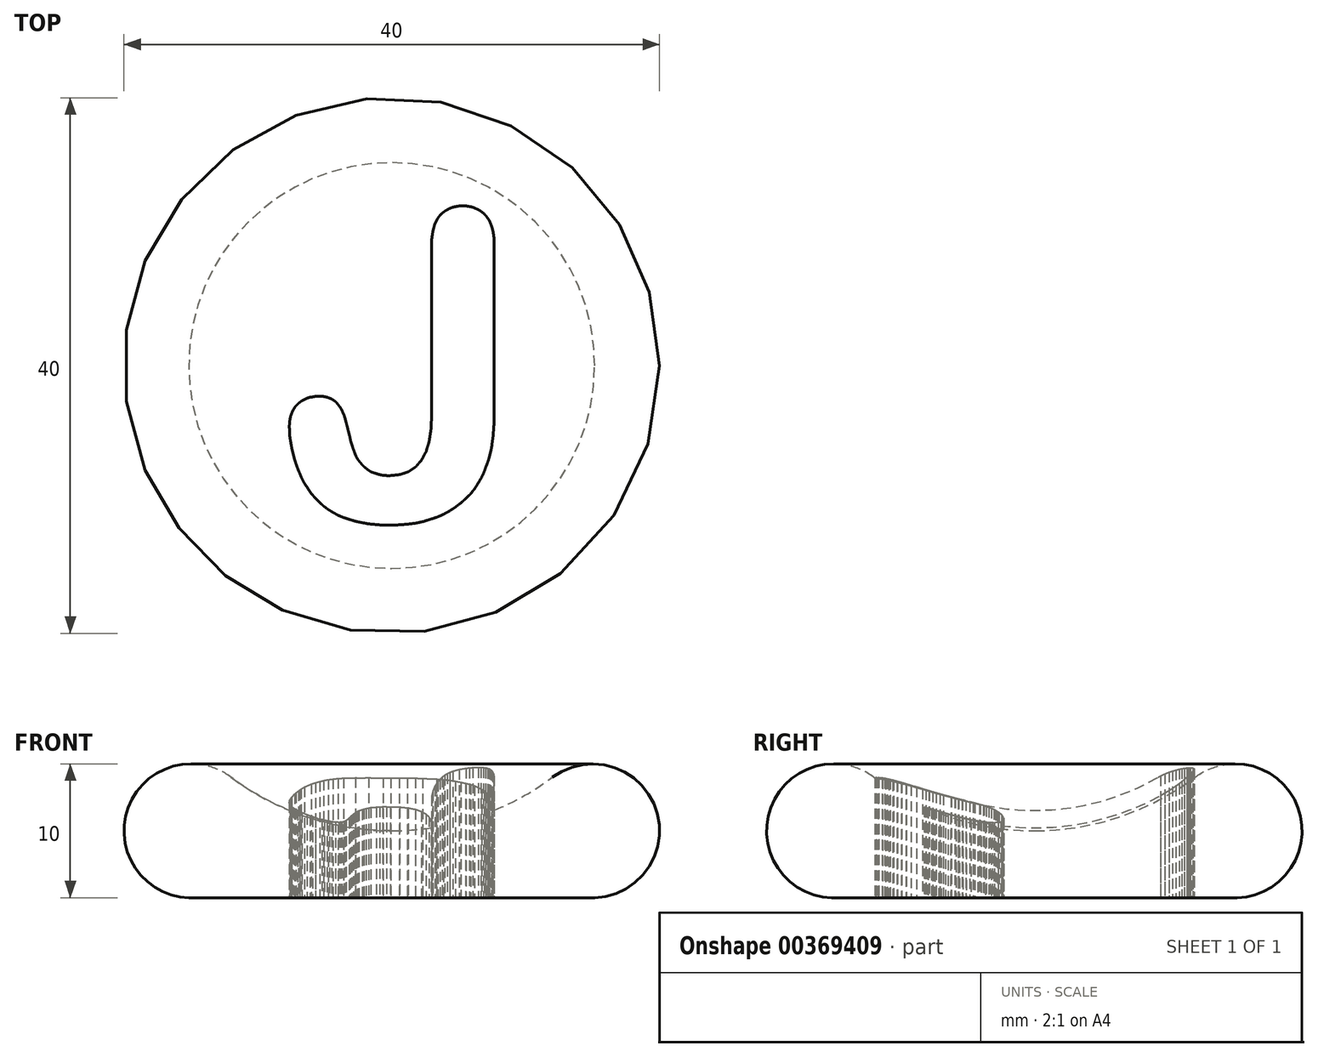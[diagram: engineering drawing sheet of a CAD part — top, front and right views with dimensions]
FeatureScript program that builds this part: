
annotation { "Feature Type Name" : "Feature", "Feature Type Description" : "" }
export const myFeature = defineFeature(function(context is Context, id is Id, definition is map)
    precondition{}
    {
        {
            var Q0;
            Q0=qCreatedBy(makeId("Front.planeOp"),FACE);
            var sketch = newSketch(context, id + "F0", { "sketchPlane" : qUnion([Q0])});
            skArc(sketch, "E0", {"start": v(-12, 9) * mm, "mid": v(-6.32, 6.03) * mm, "end": v(0, 5) * mm});
            skArc(sketch, "E1", {"start": v(-12, 9) * mm, "mid": v(-19.72, 6.65) * mm, "end": v(-15.16, 0) * mm});
            skLineSegment(sketch, "E2", {"start": v(-15.16, 0) * mm, "end": v(0, 0) * mm});
            skLineSegment(sketch, "E3", {"start": v(0, 5) * mm, "end": v(0, 0) * mm});
            skSolve(sketch);
        }
        {
            var Q0;
            Q0=makeQuery(id+"F0.imprint","IMPRINT",FACE,{"disambiguationData":[TD([[makeQuery(id+"F0.imprint","IMPRINT",EDGE,{"derivedFrom":sQuery(id+"F0.wireOp",EDGE,"E0")}),-1.0]])]});
            var Q1;
            Q1=sQuery(id+"F0.wireOp",EDGE,"E3");
            revolve(context, id + "F1", {"entities" : qUnion([Q0]), "axis" : qUnion([Q1]), "revolveType" : RevolveType.FULL});
        }
        {
            var Q0;
            Q0=qCreatedBy(makeId("Top.planeOp"),FACE);
            var sketch = newSketch(context, id + "F2", { "sketchPlane" : qUnion([Q0])});
            skLineSegment(sketch, "E4", {"start": v(-7.63, -4.3) * mm, "end": v(-7.6, -4.04) * mm});
            skLineSegment(sketch, "E5", {"start": v(-7.6, -4.04) * mm, "end": v(-7.56, -3.8) * mm});
            skLineSegment(sketch, "E6", {"start": v(-7.56, -3.8) * mm, "end": v(-7.49, -3.6) * mm});
            skLineSegment(sketch, "E7", {"start": v(-7.49, -3.6) * mm, "end": v(-7.4, -3.38) * mm});
            skLineSegment(sketch, "E8", {"start": v(-7.4, -3.38) * mm, "end": v(-7.3, -3.22) * mm});
            skLineSegment(sketch, "E9", {"start": v(-7.3, -3.22) * mm, "end": v(-7.18, -3.03) * mm});
            skLineSegment(sketch, "E10", {"start": v(-7.18, -3.03) * mm, "end": v(-7.04, -2.89) * mm});
            skLineSegment(sketch, "E11", {"start": v(-7.04, -2.89) * mm, "end": v(-6.87, -2.75) * mm});
            skLineSegment(sketch, "E12", {"start": v(-6.87, -2.75) * mm, "end": v(-6.7, -2.63) * mm});
            skLineSegment(sketch, "E13", {"start": v(-6.7, -2.63) * mm, "end": v(-6.52, -2.54) * mm});
            skLineSegment(sketch, "E14", {"start": v(-6.52, -2.54) * mm, "end": v(-6.33, -2.44) * mm});
            skLineSegment(sketch, "E15", {"start": v(-6.33, -2.44) * mm, "end": v(-6.12, -2.37) * mm});
            skLineSegment(sketch, "E16", {"start": v(-6.12, -2.37) * mm, "end": v(-5.9, -2.35) * mm});
            skLineSegment(sketch, "E17", {"start": v(-5.9, -2.35) * mm, "end": v(-5.7, -2.3) * mm});
            skLineSegment(sketch, "E18", {"start": v(-5.7, -2.3) * mm, "end": v(-5.46, -2.3) * mm});
            skLineSegment(sketch, "E19", {"start": v(-5.46, -2.3) * mm, "end": v(-5.22, -2.3) * mm});
            skLineSegment(sketch, "E20", {"start": v(-5.22, -2.3) * mm, "end": v(-5.01, -2.32) * mm});
            skLineSegment(sketch, "E21", {"start": v(-5.01, -2.32) * mm, "end": v(-4.82, -2.37) * mm});
            skLineSegment(sketch, "E22", {"start": v(-4.82, -2.37) * mm, "end": v(-4.63, -2.44) * mm});
            skLineSegment(sketch, "E23", {"start": v(-4.63, -2.44) * mm, "end": v(-4.47, -2.51) * mm});
            skLineSegment(sketch, "E24", {"start": v(-4.47, -2.51) * mm, "end": v(-4.33, -2.6) * mm});
            skLineSegment(sketch, "E25", {"start": v(-4.33, -2.6) * mm, "end": v(-4.19, -2.7) * mm});
            skLineSegment(sketch, "E26", {"start": v(-4.19, -2.7) * mm, "end": v(-4.07, -2.84) * mm});
            skLineSegment(sketch, "E27", {"start": v(-4.07, -2.84) * mm, "end": v(-3.95, -2.98) * mm});
            skLineSegment(sketch, "E28", {"start": v(-3.95, -2.98) * mm, "end": v(-3.83, -3.15) * mm});
            skLineSegment(sketch, "E29", {"start": v(-3.83, -3.15) * mm, "end": v(-3.74, -3.31) * mm});
            skLineSegment(sketch, "E30", {"start": v(-3.74, -3.31) * mm, "end": v(-3.64, -3.53) * mm});
            skLineSegment(sketch, "E31", {"start": v(-3.64, -3.53) * mm, "end": v(-3.55, -3.74) * mm});
            skLineSegment(sketch, "E32", {"start": v(-3.55, -3.74) * mm, "end": v(-3.48, -3.97) * mm});
            skLineSegment(sketch, "E33", {"start": v(-3.48, -3.97) * mm, "end": v(-3.4, -4.23) * mm});
            skLineSegment(sketch, "E34", {"start": v(-3.4, -4.23) * mm, "end": v(-3.34, -4.52) * mm});
            skLineSegment(sketch, "E35", {"start": v(-3.34, -4.52) * mm, "end": v(-3.27, -4.8) * mm});
            skLineSegment(sketch, "E36", {"start": v(-3.27, -4.8) * mm, "end": v(-3.2, -5.08) * mm});
            skLineSegment(sketch, "E37", {"start": v(-3.2, -5.08) * mm, "end": v(-3.12, -5.34) * mm});
            skLineSegment(sketch, "E38", {"start": v(-3.12, -5.34) * mm, "end": v(-3.08, -5.6) * mm});
            skLineSegment(sketch, "E39", {"start": v(-3.08, -5.6) * mm, "end": v(-3, -5.84) * mm});
            skLineSegment(sketch, "E40", {"start": v(-3, -5.84) * mm, "end": v(-2.94, -6.05) * mm});
            skLineSegment(sketch, "E41", {"start": v(-2.94, -6.05) * mm, "end": v(-2.87, -6.26) * mm});
            skLineSegment(sketch, "E42", {"start": v(-2.87, -6.26) * mm, "end": v(-2.8, -6.45) * mm});
            skLineSegment(sketch, "E43", {"start": v(-2.8, -6.45) * mm, "end": v(-2.72, -6.64) * mm});
            skLineSegment(sketch, "E44", {"start": v(-2.72, -6.64) * mm, "end": v(-2.65, -6.8) * mm});
            skLineSegment(sketch, "E45", {"start": v(-2.65, -6.8) * mm, "end": v(-2.56, -6.97) * mm});
            skLineSegment(sketch, "E46", {"start": v(-2.56, -6.97) * mm, "end": v(-2.44, -7.13) * mm});
            skLineSegment(sketch, "E47", {"start": v(-2.44, -7.13) * mm, "end": v(-2.32, -7.28) * mm});
            skLineSegment(sketch, "E48", {"start": v(-2.32, -7.28) * mm, "end": v(-2.2, -7.42) * mm});
            skLineSegment(sketch, "E49", {"start": v(-2.2, -7.42) * mm, "end": v(-2.06, -7.56) * mm});
            skLineSegment(sketch, "E50", {"start": v(-2.06, -7.56) * mm, "end": v(-1.9, -7.7) * mm});
            skLineSegment(sketch, "E51", {"start": v(-1.9, -7.7) * mm, "end": v(-1.73, -7.82) * mm});
            skLineSegment(sketch, "E52", {"start": v(-1.73, -7.82) * mm, "end": v(-1.57, -7.94) * mm});
            skLineSegment(sketch, "E53", {"start": v(-1.57, -7.94) * mm, "end": v(-1.36, -8) * mm});
            skLineSegment(sketch, "E54", {"start": v(-1.36, -8) * mm, "end": v(-1.14, -8.08) * mm});
            skLineSegment(sketch, "E55", {"start": v(-1.14, -8.08) * mm, "end": v(-0.9, -8.15) * mm});
            skLineSegment(sketch, "E56", {"start": v(-0.9, -8.15) * mm, "end": v(-0.67, -8.2) * mm});
            skLineSegment(sketch, "E57", {"start": v(-0.67, -8.2) * mm, "end": v(-0.39, -8.22) * mm});
            skLineSegment(sketch, "E58", {"start": v(-0.39, -8.22) * mm, "end": v(-0.1, -8.22) * mm});
            skLineSegment(sketch, "E59", {"start": v(-0.1, -8.22) * mm, "end": v(0.6, -8.15) * mm});
            skLineSegment(sketch, "E60", {"start": v(0.6, -8.15) * mm, "end": v(1.24, -7.94) * mm});
            skLineSegment(sketch, "E61", {"start": v(1.24, -7.94) * mm, "end": v(1.78, -7.58) * mm});
            skLineSegment(sketch, "E62", {"start": v(1.78, -7.58) * mm, "end": v(2.2, -7.09) * mm});
            skLineSegment(sketch, "E63", {"start": v(2.2, -7.09) * mm, "end": v(2.56, -6.45) * mm});
            skLineSegment(sketch, "E64", {"start": v(2.56, -6.45) * mm, "end": v(2.8, -5.67) * mm});
            skLineSegment(sketch, "E65", {"start": v(2.8, -5.67) * mm, "end": v(2.94, -4.73) * mm});
            skLineSegment(sketch, "E66", {"start": v(2.94, -4.73) * mm, "end": v(2.98, -3.67) * mm});
            skLineSegment(sketch, "E67", {"start": v(2.98, -3.67) * mm, "end": v(2.98, 9.1) * mm});
            skLineSegment(sketch, "E68", {"start": v(2.98, 9.1) * mm, "end": v(2.98, 9.42) * mm});
            skLineSegment(sketch, "E69", {"start": v(2.98, 9.42) * mm, "end": v(3.03, 9.75) * mm});
            skLineSegment(sketch, "E70", {"start": v(3.03, 9.75) * mm, "end": v(3.08, 10.06) * mm});
            skLineSegment(sketch, "E71", {"start": v(3.08, 10.06) * mm, "end": v(3.15, 10.32) * mm});
            skLineSegment(sketch, "E72", {"start": v(3.15, 10.32) * mm, "end": v(3.22, 10.58) * mm});
            skLineSegment(sketch, "E73", {"start": v(3.22, 10.58) * mm, "end": v(3.34, 10.81) * mm});
            skLineSegment(sketch, "E74", {"start": v(3.34, 10.81) * mm, "end": v(3.46, 11.03) * mm});
            skLineSegment(sketch, "E75", {"start": v(3.46, 11.03) * mm, "end": v(3.6, 11.21) * mm});
            skLineSegment(sketch, "E76", {"start": v(3.6, 11.21) * mm, "end": v(3.76, 11.38) * mm});
            skLineSegment(sketch, "E77", {"start": v(3.76, 11.38) * mm, "end": v(3.95, 11.52) * mm});
            skLineSegment(sketch, "E78", {"start": v(3.95, 11.52) * mm, "end": v(4.14, 11.64) * mm});
            skLineSegment(sketch, "E79", {"start": v(4.14, 11.64) * mm, "end": v(4.33, 11.73) * mm});
            skLineSegment(sketch, "E80", {"start": v(4.33, 11.73) * mm, "end": v(4.56, 11.83) * mm});
            skLineSegment(sketch, "E81", {"start": v(4.56, 11.83) * mm, "end": v(4.8, 11.87) * mm});
            skLineSegment(sketch, "E82", {"start": v(4.8, 11.87) * mm, "end": v(5.04, 11.92) * mm});
            skLineSegment(sketch, "E83", {"start": v(5.04, 11.92) * mm, "end": v(5.3, 11.92) * mm});
            skLineSegment(sketch, "E84", {"start": v(5.3, 11.92) * mm, "end": v(5.55, 11.92) * mm});
            skLineSegment(sketch, "E85", {"start": v(5.55, 11.92) * mm, "end": v(5.81, 11.87) * mm});
            skLineSegment(sketch, "E86", {"start": v(5.81, 11.87) * mm, "end": v(6.05, 11.83) * mm});
            skLineSegment(sketch, "E87", {"start": v(6.05, 11.83) * mm, "end": v(6.26, 11.73) * mm});
            skLineSegment(sketch, "E88", {"start": v(6.26, 11.73) * mm, "end": v(6.47, 11.64) * mm});
            skLineSegment(sketch, "E89", {"start": v(6.47, 11.64) * mm, "end": v(6.66, 11.52) * mm});
            skLineSegment(sketch, "E90", {"start": v(6.66, 11.52) * mm, "end": v(6.85, 11.38) * mm});
            skLineSegment(sketch, "E91", {"start": v(6.85, 11.38) * mm, "end": v(7.02, 11.21) * mm});
            skLineSegment(sketch, "E92", {"start": v(7.02, 11.21) * mm, "end": v(7.16, 11.03) * mm});
            skLineSegment(sketch, "E93", {"start": v(7.16, 11.03) * mm, "end": v(7.3, 10.81) * mm});
            skLineSegment(sketch, "E94", {"start": v(7.3, 10.81) * mm, "end": v(7.4, 10.58) * mm});
            skLineSegment(sketch, "E95", {"start": v(7.4, 10.58) * mm, "end": v(7.49, 10.32) * mm});
            skLineSegment(sketch, "E96", {"start": v(7.49, 10.32) * mm, "end": v(7.56, 10.06) * mm});
            skLineSegment(sketch, "E97", {"start": v(7.56, 10.06) * mm, "end": v(7.6, 9.75) * mm});
            skLineSegment(sketch, "E98", {"start": v(7.6, 9.75) * mm, "end": v(7.65, 9.42) * mm});
            skLineSegment(sketch, "E99", {"start": v(7.65, 9.42) * mm, "end": v(7.65, 9.1) * mm});
            skLineSegment(sketch, "E100", {"start": v(7.65, 9.1) * mm, "end": v(7.65, -2.98) * mm});
            skLineSegment(sketch, "E101", {"start": v(7.65, -2.98) * mm, "end": v(7.65, -3.38) * mm});
            skLineSegment(sketch, "E102", {"start": v(7.65, -3.38) * mm, "end": v(7.65, -3.74) * mm});
            skLineSegment(sketch, "E103", {"start": v(7.65, -3.74) * mm, "end": v(7.63, -4.1) * mm});
            skLineSegment(sketch, "E104", {"start": v(7.63, -4.1) * mm, "end": v(7.63, -4.45) * mm});
            skLineSegment(sketch, "E105", {"start": v(7.63, -4.45) * mm, "end": v(7.6, -4.78) * mm});
            skLineSegment(sketch, "E106", {"start": v(7.6, -4.78) * mm, "end": v(7.58, -5.08) * mm});
            skLineSegment(sketch, "E107", {"start": v(7.58, -5.08) * mm, "end": v(7.56, -5.39) * mm});
            skLineSegment(sketch, "E108", {"start": v(7.56, -5.39) * mm, "end": v(7.51, -5.67) * mm});
            skLineSegment(sketch, "E109", {"start": v(7.51, -5.67) * mm, "end": v(7.49, -5.93) * mm});
            skLineSegment(sketch, "E110", {"start": v(7.49, -5.93) * mm, "end": v(7.44, -6.21) * mm});
            skLineSegment(sketch, "E111", {"start": v(7.44, -6.21) * mm, "end": v(7.37, -6.5) * mm});
            skLineSegment(sketch, "E112", {"start": v(7.37, -6.5) * mm, "end": v(7.3, -6.78) * mm});
            skLineSegment(sketch, "E113", {"start": v(7.3, -6.78) * mm, "end": v(7.23, -7.04) * mm});
            skLineSegment(sketch, "E114", {"start": v(7.23, -7.04) * mm, "end": v(7.13, -7.32) * mm});
            skLineSegment(sketch, "E115", {"start": v(7.13, -7.32) * mm, "end": v(7.02, -7.6) * mm});
            skLineSegment(sketch, "E116", {"start": v(7.02, -7.6) * mm, "end": v(6.92, -7.89) * mm});
            skLineSegment(sketch, "E117", {"start": v(6.92, -7.89) * mm, "end": v(6.7, -8.36) * mm});
            skLineSegment(sketch, "E118", {"start": v(6.7, -8.36) * mm, "end": v(6.45, -8.79) * mm});
            skLineSegment(sketch, "E119", {"start": v(6.45, -8.79) * mm, "end": v(6.2, -9.2) * mm});
            skLineSegment(sketch, "E120", {"start": v(6.2, -9.2) * mm, "end": v(5.88, -9.59) * mm});
            skLineSegment(sketch, "E121", {"start": v(5.88, -9.59) * mm, "end": v(5.53, -9.94) * mm});
            skLineSegment(sketch, "E122", {"start": v(5.53, -9.94) * mm, "end": v(5.15, -10.27) * mm});
            skLineSegment(sketch, "E123", {"start": v(5.15, -10.27) * mm, "end": v(4.75, -10.58) * mm});
            skLineSegment(sketch, "E124", {"start": v(4.75, -10.58) * mm, "end": v(4.33, -10.86) * mm});
            skLineSegment(sketch, "E125", {"start": v(4.33, -10.86) * mm, "end": v(3.86, -11.12) * mm});
            skLineSegment(sketch, "E126", {"start": v(3.86, -11.12) * mm, "end": v(3.36, -11.33) * mm});
            skLineSegment(sketch, "E127", {"start": v(3.36, -11.33) * mm, "end": v(2.84, -11.5) * mm});
            skLineSegment(sketch, "E128", {"start": v(2.84, -11.5) * mm, "end": v(2.32, -11.66) * mm});
            skLineSegment(sketch, "E129", {"start": v(2.32, -11.66) * mm, "end": v(1.76, -11.78) * mm});
            skLineSegment(sketch, "E130", {"start": v(1.76, -11.78) * mm, "end": v(1.17, -11.85) * mm});
            skLineSegment(sketch, "E131", {"start": v(1.17, -11.85) * mm, "end": v(0.55, -11.9) * mm});
            skLineSegment(sketch, "E132", {"start": v(0.55, -11.9) * mm, "end": v(-0.08, -11.92) * mm});
            skLineSegment(sketch, "E133", {"start": v(-0.08, -11.92) * mm, "end": v(-0.65, -11.92) * mm});
            skLineSegment(sketch, "E134", {"start": v(-0.65, -11.92) * mm, "end": v(-1.21, -11.87) * mm});
            skLineSegment(sketch, "E135", {"start": v(-1.21, -11.87) * mm, "end": v(-1.73, -11.83) * mm});
            skLineSegment(sketch, "E136", {"start": v(-1.73, -11.83) * mm, "end": v(-2.23, -11.73) * mm});
            skLineSegment(sketch, "E137", {"start": v(-2.23, -11.73) * mm, "end": v(-2.7, -11.64) * mm});
            skLineSegment(sketch, "E138", {"start": v(-2.7, -11.64) * mm, "end": v(-3.15, -11.5) * mm});
            skLineSegment(sketch, "E139", {"start": v(-3.15, -11.5) * mm, "end": v(-3.6, -11.36) * mm});
            skLineSegment(sketch, "E140", {"start": v(-3.6, -11.36) * mm, "end": v(-4, -11.2) * mm});
            skLineSegment(sketch, "E141", {"start": v(-4, -11.2) * mm, "end": v(-4.37, -10.98) * mm});
            skLineSegment(sketch, "E142", {"start": v(-4.37, -10.98) * mm, "end": v(-4.73, -10.77) * mm});
            skLineSegment(sketch, "E143", {"start": v(-4.73, -10.77) * mm, "end": v(-5.08, -10.5) * mm});
            skLineSegment(sketch, "E144", {"start": v(-5.08, -10.5) * mm, "end": v(-5.39, -10.22) * mm});
            skLineSegment(sketch, "E145", {"start": v(-5.39, -10.22) * mm, "end": v(-5.7, -9.92) * mm});
            skLineSegment(sketch, "E146", {"start": v(-5.7, -9.92) * mm, "end": v(-6, -9.56) * mm});
            skLineSegment(sketch, "E147", {"start": v(-6, -9.56) * mm, "end": v(-6.26, -9.19) * mm});
            skLineSegment(sketch, "E148", {"start": v(-6.26, -9.19) * mm, "end": v(-6.52, -8.8) * mm});
            skLineSegment(sketch, "E149", {"start": v(-6.52, -8.8) * mm, "end": v(-6.64, -8.57) * mm});
            skLineSegment(sketch, "E150", {"start": v(-6.64, -8.57) * mm, "end": v(-6.76, -8.34) * mm});
            skLineSegment(sketch, "E151", {"start": v(-6.76, -8.34) * mm, "end": v(-6.85, -8.1) * mm});
            skLineSegment(sketch, "E152", {"start": v(-6.85, -8.1) * mm, "end": v(-6.97, -7.84) * mm});
            skLineSegment(sketch, "E153", {"start": v(-6.97, -7.84) * mm, "end": v(-7.06, -7.58) * mm});
            skLineSegment(sketch, "E154", {"start": v(-7.06, -7.58) * mm, "end": v(-7.16, -7.32) * mm});
            skLineSegment(sketch, "E155", {"start": v(-7.16, -7.32) * mm, "end": v(-7.25, -7.04) * mm});
            skLineSegment(sketch, "E156", {"start": v(-7.25, -7.04) * mm, "end": v(-7.32, -6.76) * mm});
            skLineSegment(sketch, "E157", {"start": v(-7.32, -6.76) * mm, "end": v(-7.4, -6.47) * mm});
            skLineSegment(sketch, "E158", {"start": v(-7.4, -6.47) * mm, "end": v(-7.46, -6.2) * mm});
            skLineSegment(sketch, "E159", {"start": v(-7.46, -6.2) * mm, "end": v(-7.51, -5.9) * mm});
            skLineSegment(sketch, "E160", {"start": v(-7.51, -5.9) * mm, "end": v(-7.56, -5.65) * mm});
            skLineSegment(sketch, "E161", {"start": v(-7.56, -5.65) * mm, "end": v(-7.6, -5.37) * mm});
            skLineSegment(sketch, "E162", {"start": v(-7.6, -5.37) * mm, "end": v(-7.63, -5.1) * mm});
            skLineSegment(sketch, "E163", {"start": v(-7.63, -5.1) * mm, "end": v(-7.63, -4.82) * mm});
            skLineSegment(sketch, "E164", {"start": v(-7.63, -4.82) * mm, "end": v(-7.65, -4.56) * mm});
            skLineSegment(sketch, "E165", {"start": v(-7.65, -4.56) * mm, "end": v(-7.63, -4.3) * mm});
            skSolve(sketch);
        }
        {
            var Q0;
            Q0 = qSketchRegion(id + "F2", true);
            extrude(context, id + "F3", {"entities" : qUnion([Q0]), "operationType" : NewBodyOperationType.REMOVE, "oppositeDirection" : true, "depth" : -25.4 * mm});
        }
    });
